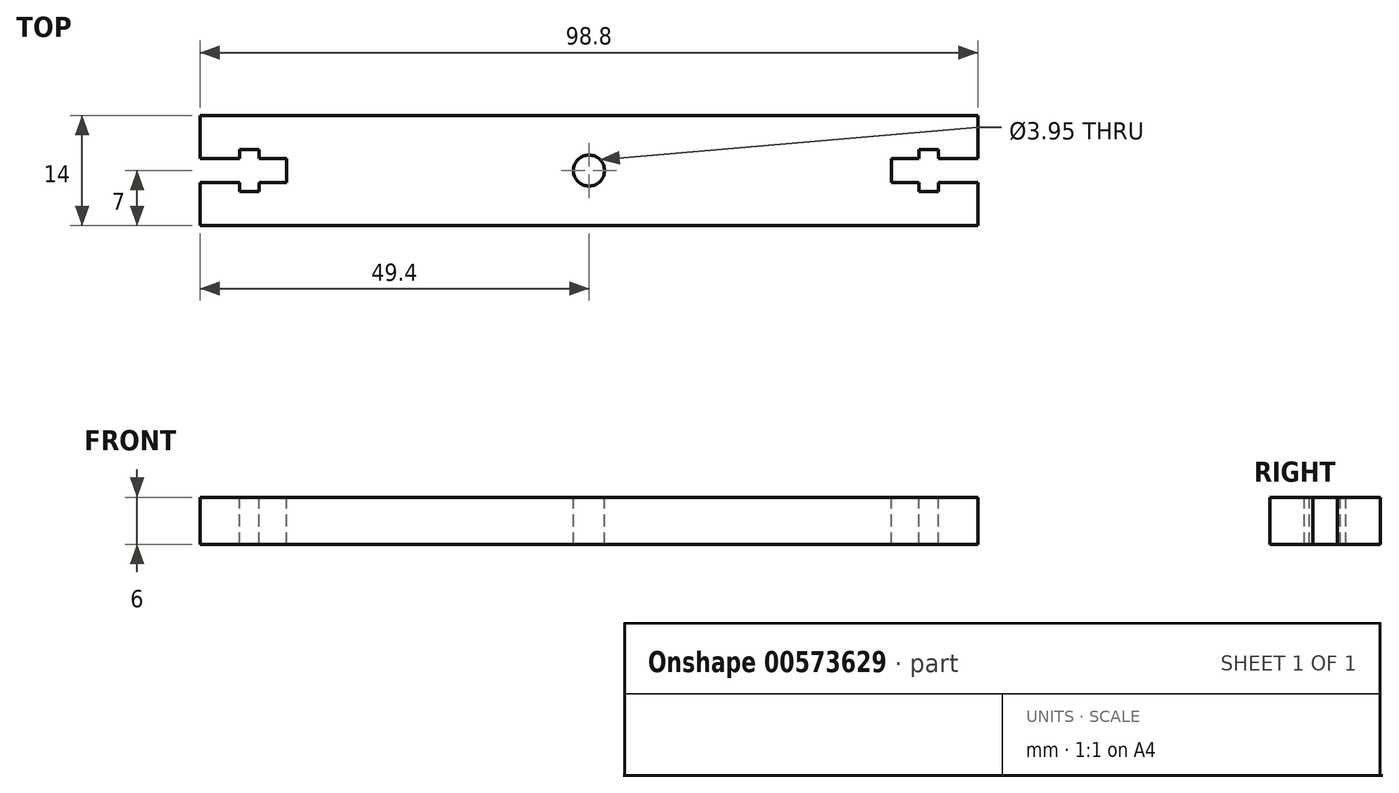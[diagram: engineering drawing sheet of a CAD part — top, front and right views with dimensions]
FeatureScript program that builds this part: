
annotation { "Feature Type Name" : "Feature", "Feature Type Description" : "" }
export const myFeature = defineFeature(function(context is Context, id is Id, definition is map)
    precondition{}
    {
        {
            var Q0;
            Q0=qCreatedBy(makeId("Top.planeOp"),FACE);
            var sketch = newSketch(context, id + "F0", { "sketchPlane" : qUnion([Q0])});
            skLineSegment(sketch, "E0.bottom", {"start": v(49.4, -7) * mm, "end": v(-49.4, -7) * mm});
            skLineSegment(sketch, "E0.top", {"start": v(49.4, 7) * mm, "end": v(-49.4, 7) * mm});
            skLineSegment(sketch, "E0.left", {"start": v(49.4, -7) * mm, "end": v(49.4, 7) * mm});
            skLineSegment(sketch, "E0.right", {"start": v(-49.4, -7) * mm, "end": v(-49.4, 7) * mm});
            skPoint(sketch, "E0.middle", {"position": v(0, 0) * mm});
            skSolve(sketch);
        }
        {
            var Q0;
            Q0=qSketchRegion(id+"F0",true);
            extrude(context, id + "F1", {"entities" : qUnion([Q0]), "depth" : 6 * mm, "offsetDistance" : 25 * mm});
        }
        {
            var Q0;
            Q0=makeQuery(id+"F1.opExtrude","CAP_FACE",FACE,{"disambiguationData":[OSD([sQuery(id+"F0.wireOp",EDGE,"E0.bottom"),sQuery(id+"F0.wireOp",EDGE,"E0.top"),sQuery(id+"F0.wireOp",EDGE,"E0.left"),sQuery(id+"F0.wireOp",EDGE,"E0.right")])],"isStart":false});
            var sketch = newSketch(context, id + "F2", { "sketchPlane" : qUnion([Q0])});
            skLineSegment(sketch, "E1", {"start": v(-49.4, 0) * mm, "end": v(49.4, 0) * mm, "construction": true});
            skLineSegment(sketch, "E2", {"start": v(0, 7) * mm, "end": v(0, -7) * mm, "construction": true});
            skLineSegment(sketch, "E3.bottom", {"start": v(-49.4, -1.55) * mm, "end": v(-38.4, -1.55) * mm});
            skLineSegment(sketch, "E3.top", {"start": v(-49.4, 1.55) * mm, "end": v(-38.4, 1.55) * mm});
            skLineSegment(sketch, "E3.left", {"start": v(-49.4, -1.55) * mm, "end": v(-49.4, 1.55) * mm});
            skLineSegment(sketch, "E3.right", {"start": v(-38.4, -1.55) * mm, "end": v(-38.4, 1.55) * mm});
            skLineSegment(sketch, "E4", {"start": v(-49.4, 0) * mm, "end": v(-38.4, 0) * mm, "construction": true});
            skLineSegment(sketch, "E5.bottom", {"start": v(-41.9, -2.65) * mm, "end": v(-44.4, -2.65) * mm});
            skLineSegment(sketch, "E5.top", {"start": v(-41.9, 2.65) * mm, "end": v(-44.4, 2.65) * mm});
            skLineSegment(sketch, "E5.left", {"start": v(-41.9, -2.65) * mm, "end": v(-41.9, 2.65) * mm});
            skLineSegment(sketch, "E5.right", {"start": v(-44.4, -2.65) * mm, "end": v(-44.4, 2.65) * mm});
            skPoint(sketch, "E5.middle", {"position": v(-43.15, 0) * mm});
            skLineSegment(sketch, "E6.MirrorCS", {"start": v(49.4, -1.55) * mm, "end": v(49.4, 1.55) * mm});
            skLineSegment(sketch, "E7.MirrorCS", {"start": v(38.4, -1.55) * mm, "end": v(38.4, 1.55) * mm});
            skLineSegment(sketch, "E8.MirrorCS", {"start": v(41.9, 2.65) * mm, "end": v(44.4, 2.65) * mm});
            skLineSegment(sketch, "E9.MirrorCS", {"start": v(41.9, -2.65) * mm, "end": v(44.4, -2.65) * mm});
            skLineSegment(sketch, "E10.MirrorCS", {"start": v(41.9, -2.65) * mm, "end": v(41.9, 2.65) * mm});
            skPoint(sketch, "E11.MirrorP", {"position": v(43.15, 0) * mm});
            skLineSegment(sketch, "E12.MirrorCS", {"start": v(49.4, 1.55) * mm, "end": v(38.4, 1.55) * mm});
            skLineSegment(sketch, "E13.MirrorCS", {"start": v(44.4, -2.65) * mm, "end": v(44.4, 2.65) * mm});
            skLineSegment(sketch, "E14.MirrorCS", {"start": v(49.4, -1.55) * mm, "end": v(38.4, -1.55) * mm});
            skSolve(sketch);
        }
        {
            var Q0;
            Q0=qSketchRegion(id+"F2",true);
            var Q1;
            Q1=makeQuery(id+"F1.opExtrude","CAP_FACE",FACE,{"disambiguationData":[OSD([sQuery(id+"F0.wireOp",EDGE,"E0.bottom"),sQuery(id+"F0.wireOp",EDGE,"E0.top"),sQuery(id+"F0.wireOp",EDGE,"E0.left"),sQuery(id+"F0.wireOp",EDGE,"E0.right")])],"isStart":true});
            extrude(context, id + "F3", {"entities" : qUnion([Q0]), "operationType" : NewBodyOperationType.REMOVE, "endBound" : BoundingType.UP_TO_SURFACE, "oppositeDirection" : true, "depth" : 25 * mm, "endBoundEntityFace" : qUnion([Q1]), "offsetDistance" : 25 * mm});
        }
        {
            var Q0;
            Q0=makeQuery(id+"F1.opExtrude","CAP_FACE",FACE,{"disambiguationData":[OSD([sQuery(id+"F0.wireOp",EDGE,"E0.bottom"),sQuery(id+"F0.wireOp",EDGE,"E0.top"),sQuery(id+"F0.wireOp",EDGE,"E0.left"),sQuery(id+"F0.wireOp",EDGE,"E0.right")])],"isStart":false});
            var sketch = newSketch(context, id + "F4", { "sketchPlane" : qUnion([Q0])});
            skCircle(sketch, "E15", {"center": v(0, 0) * mm, "radius": 1.98 * mm});
            skSolve(sketch);
        }
        {
            var Q0;
            Q0=qSketchRegion(id+"F4",true);
            var Q1;
            Q1=makeQuery(id+"F1.opExtrude","CAP_FACE",FACE,{"disambiguationData":[OSD([sQuery(id+"F0.wireOp",EDGE,"E0.bottom"),sQuery(id+"F0.wireOp",EDGE,"E0.top"),sQuery(id+"F0.wireOp",EDGE,"E0.left"),sQuery(id+"F0.wireOp",EDGE,"E0.right")])],"isStart":true});
            extrude(context, id + "F5", {"entities" : qUnion([Q0]), "operationType" : NewBodyOperationType.REMOVE, "endBound" : BoundingType.UP_TO_SURFACE, "oppositeDirection" : true, "depth" : 25 * mm, "endBoundEntityFace" : qUnion([Q1]), "offsetDistance" : 25 * mm});
        }
    });
